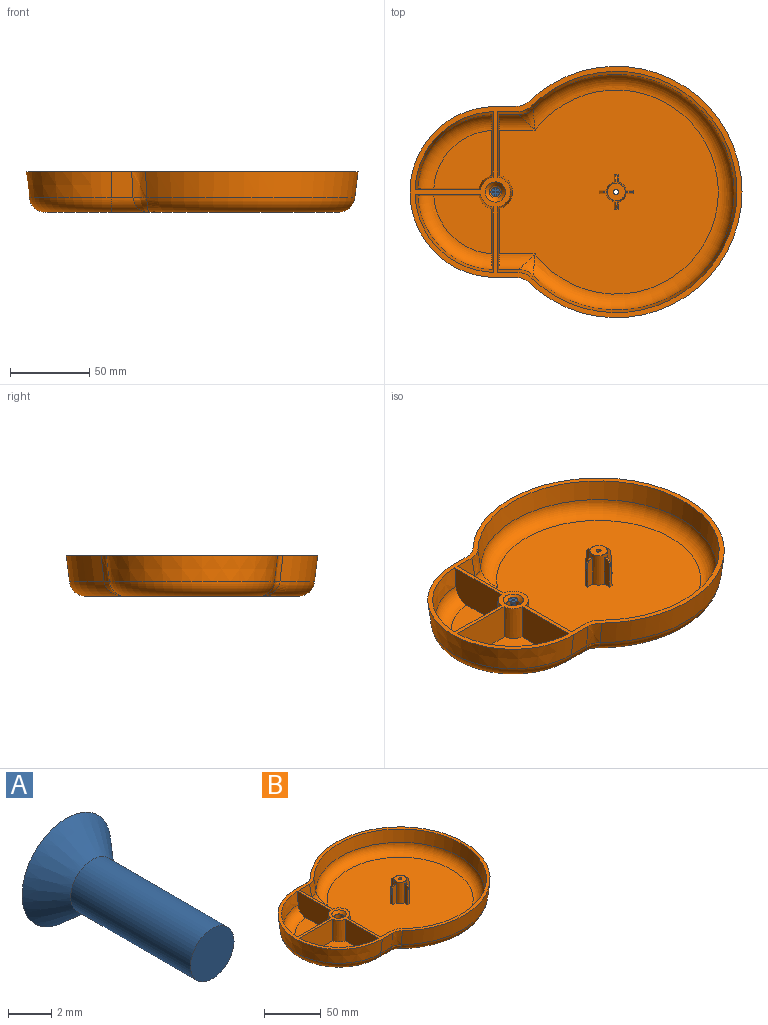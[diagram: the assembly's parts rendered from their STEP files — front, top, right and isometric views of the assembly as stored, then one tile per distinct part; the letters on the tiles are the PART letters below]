
ASSEMBLY  parts=2 mates=1
PART A: 17 faces, bbox 5.8x9.5x5.8 mm
  f0: plane 5.8x5.8mm, normal (0,1,0), area 20.5mm2, adj f1,f2,f5,f6,f8,f9,f10,f11
  f1: plane 1.78x0.38mm, normal (-1,0,0), area 0.7mm2, adj f0,f6,f7,f8
  f2: plane 1.78x0.38mm, normal (1,0,0), area 0.7mm2, adj f0,f6,f7,f10
  f3: plane 2.85x2.85mm, normal (0,-1,0), area 6.4mm2, adj f4
  f4: cylinder r=1.42mm len=7.82mm, axis (0,1,0), area 69.9mm2, adj f3,f5
  f5: cone r=1.42mm half-angle=41deg, axis (0,1,0), area 30.6mm2, adj f0,f4
  f6: plane 0.76x0.38mm, normal (0,0,-1), area 0.3mm2, adj f0,f1,f2,f7
  f7: plane 4.32x4.32mm, normal (0,1,0), area 6mm2, adj f1,f2,f6,f8,f9,f10,f11,f12
  f8: plane 1.78x0.38mm, normal (0,0,-1), area 0.7mm2, adj f0,f1,f7,f16
  f9: plane 1.78x0.38mm, normal (0,0,1), area 0.7mm2, adj f0,f7,f11,f12
  f10: plane 1.78x0.38mm, normal (0,0,-1), area 0.7mm2, adj f0,f2,f7,f11
  f11: plane 0.76x0.38mm, normal (1,0,0), area 0.3mm2, adj f0,f7,f9,f10
  f12: plane 1.78x0.38mm, normal (1,0,0), area 0.7mm2, adj f0,f7,f9,f14
  f13: plane 1.78x0.38mm, normal (-1,0,0), area 0.7mm2, adj f0,f7,f14,f15
  f14: plane 0.76x0.38mm, normal (0,0,1), area 0.3mm2, adj f0,f7,f12,f13
  f15: plane 1.78x0.38mm, normal (0,0,1), area 0.7mm2, adj f0,f7,f13,f16
  f16: plane 0.76x0.38mm, normal (-1,0,0), area 0.3mm2, adj f0,f7,f8,f15
PART B: 68 faces, bbox 216.5x167.7x161.1 mm
  f0: cone r=47.65mm half-angle=7deg, axis (0,0,1), area 1007.1mm2, adj f1,f12,f34,f38
  f1: torus R=39mm, axis (0,0,1), area 976.5mm2, adj f0,f2,f34,f38
  f2: plane 36.49x36.49mm, normal (0,0,1), area 966.8mm2, adj f1,f3,f34,f38
  f3: cone r=9.53mm half-angle=3deg, axis (0,0,-1), area 271.2mm2, adj f2,f12,f34,f38
  f4: cone r=47.65mm half-angle=7deg, axis (0,0,1), area 1007.1mm2, adj f6,f12,f35,f37
  f5: plane 36.49x36.49mm, normal (0,0,1), area 966.8mm2, adj f6,f7,f35,f37
  f6: torus R=39mm, axis (0,0,1), area 976.5mm2, adj f4,f5,f35,f37
  f7: cone r=9.53mm half-angle=3deg, axis (0,0,-1), area 271.2mm2, adj f5,f12,f35,f37
  f8: plane 16.48x13.58mm, normal (0,-0.99,-0.12), area 218.6mm2, adj f11,f12,f18,f29
  f9: cone r=76.2mm half-angle=7deg, axis (0,0,1), area 6076.3mm2, adj f12,f20,f29,f31
  f10: plane 16.48x13.58mm, normal (0,0.99,-0.12), area 218.6mm2, adj f11,f12,f21,f31
  f11: cone r=50.8mm half-angle=7deg, axis (0,0,1), area 2759.5mm2, adj f8,f10,f12,f19
  f12: plane 209.69x158.89mm, normal (0,0,1), area 2312.5mm2, adj f0,f3,f4,f7,f8,f9,f10,f11
  f13: plane 185.22x134.42mm, normal (0,0,-1), area 18002.1mm2, adj f18,f19,f20,f21,f65
  f14: plane 13.46x13.3mm, normal (0,0.99,0.12), area 171.2mm2, adj f12,f24,f27,f39
  f15: cone r=73.05mm half-angle=7deg, axis (0,0,1), area 4744.9mm2, adj f12,f22,f25,f27
  f16: plane 13.46x13.3mm, normal (0,-0.99,0.12), area 171.2mm2, adj f12,f23,f25,f36
  f17: plane 138.17x128.8mm, normal (0,0,1), area 13789.8mm2, adj f22,f23,f24,f33,f36,f39,f43,f45
  f18: cylinder r=10.16mm len=23.58mm, axis (-1,0,0), area 273.4mm2, adj f8,f13,f19,f30
  f19: torus R=41.81mm, axis (0,0,1), area 2218mm2, adj f11,f13,f18,f21
  f20: torus R=67.21mm, axis (0,0,1), area 5192.6mm2, adj f9,f13,f30,f32
  f21: cylinder r=10.16mm len=23.58mm, axis (-1,0,0), area 273.4mm2, adj f10,f13,f19,f32
  f22: torus R=64.4mm, axis (0,0,1), area 5028.6mm2, adj f15,f17,f26,f28
  f23: cylinder r=10.16mm len=22.98mm, axis (1,0,0), area 259.6mm2, adj f16,f17,f26,f36
  f24: cylinder r=10.16mm len=22.98mm, axis (1,0,0), area 259.6mm2, adj f14,f17,f28,f39
  f25: bspline ~126.22x18.65mm, area 131.8mm2, adj f12,f15,f16,f26
  f26: bspline ~13.84x10.28mm, area 60.5mm2, adj f22,f23,f25
  f27: bspline ~155.52x22.25mm, area 131.8mm2, adj f12,f14,f15,f28
  f28: bspline ~13.84x10.28mm, area 60.5mm2, adj f22,f24,f27
  f29: bspline ~130.53x19.08mm, area 160.5mm2, adj f8,f9,f12,f30
  f30: bspline ~13.73x10.06mm, area 59.3mm2, adj f18,f20,f29
  f31: bspline ~160.83x22.8mm, area 160.4mm2, adj f9,f10,f12,f32
  f32: bspline ~13.73x10.06mm, area 59.3mm2, adj f20,f21,f31
  f33: cone r=9.53mm half-angle=3deg, axis (0,0,-1), area 624.5mm2, adj f12,f17,f36,f39
  f34: plane 41.36x22.32mm, normal (0,-1,0.05), area 860mm2, adj f0,f1,f2,f3,f12
  f35: plane 41.36x22.32mm, normal (0,1,0.05), area 860mm2, adj f4,f5,f6,f7,f12
  f36: plane 41.48x22.43mm, normal (1,0,0.05), area 860.8mm2, adj f12,f16,f17,f23,f33
  f37: plane 41.36x22.32mm, normal (-1,0,0.05), area 860mm2, adj f4,f5,f6,f7,f12
  f38: plane 41.36x22.32mm, normal (-1,0,0.05), area 860mm2, adj f0,f1,f2,f3,f12
  f39: plane 41.48x22.43mm, normal (1,0,0.05), area 860.8mm2, adj f12,f14,f17,f24,f33
  f40: cone r=0mm half-angle=59deg, axis (0,0,1), area 59mm2, adj f41
  f41: cylinder r=4.01mm len=16.36mm, axis (0,0,1), area 412.6mm2, adj f40,f42
  f42: cone r=4.01mm half-angle=41deg, axis (0,0,1), area 116mm2, adj f12,f41
  f43: cone r=5.56mm half-angle=2deg, axis (0,0,-1), area 697.6mm2, adj f17,f44,f45,f46,f47,f49,f50,f51
  f44: plane 11.11x11.11mm, normal (0,0,1), area 89.1mm2, adj f43,f67
  f45: plane 19.72x5.26mm, normal (1,0,0.03), area 88.1mm2, adj f17,f43,f47,f48,f64
  f46: plane 19.72x5.26mm, normal (-1,0,0.03), area 88.1mm2, adj f17,f43,f47,f48,f64
  f47: plane 2.51x1.02mm, normal (0,0,1), area 2.5mm2, adj f43,f45,f46,f64
  f48: plane 17.65x2.39mm, normal (0,1,0.03), area 31.3mm2, adj f17,f45,f46,f64
  f49: plane 2.51x1.02mm, normal (0,0,1), area 2.5mm2, adj f43,f50,f51,f61
  f50: plane 19.72x5.26mm, normal (0,-1,0.03), area 88.1mm2, adj f17,f43,f49,f52,f61
  f51: plane 19.72x5.26mm, normal (0,1,0.03), area 88.1mm2, adj f17,f43,f49,f52,f61
  f52: plane 17.65x2.39mm, normal (1,0,0.03), area 31.3mm2, adj f17,f50,f51,f61
  f53: plane 2.51x1.02mm, normal (0,0,1), area 2.5mm2, adj f43,f54,f55,f63
  f54: plane 19.72x5.26mm, normal (0,1,0.03), area 88.1mm2, adj f17,f43,f53,f56,f63
  f55: plane 19.72x5.26mm, normal (0,-1,0.03), area 88.1mm2, adj f17,f43,f53,f56,f63
  f56: plane 17.65x2.39mm, normal (-1,0,0.03), area 31.3mm2, adj f17,f54,f55,f63
  f57: plane 2.51x1.02mm, normal (0,0,1), area 2.5mm2, adj f43,f58,f60,f62
  f58: plane 19.72x5.26mm, normal (1,0,0.03), area 88.1mm2, adj f17,f43,f57,f59,f62
  f59: plane 17.65x2.39mm, normal (0,-1,0.03), area 31.3mm2, adj f17,f58,f60,f62
  f60: plane 19.72x5.26mm, normal (-1,0,0.03), area 88.1mm2, adj f17,f43,f57,f59,f62
  f61: plane 2.1x2.03mm, normal (0.69,0,0.72), area 3.2mm2, adj f49,f50,f51,f52
  f62: plane 2.1x2.03mm, normal (0,-0.69,0.72), area 3.2mm2, adj f57,f58,f59,f60
  f63: plane 2.1x2.03mm, normal (-0.69,0,0.72), area 3.2mm2, adj f53,f54,f55,f56
  f64: plane 2.1x2.03mm, normal (0,0.69,0.72), area 3.2mm2, adj f45,f46,f47,f48
  f65: cone r=4.03mm half-angle=2deg, axis (0,0,-1), area 667.9mm2, adj f13,f66
  f66: plane 8.06x8.06mm, normal (0,0,-1), area 42.6mm2, adj f65,f67
  f67: cone r=1.59mm half-angle=2deg, axis (0,0,-1), area 15.5mm2, adj f44,f66
PLACE A rot(axis=(1,0,0),90deg) t=(0,0,15.88)mm
PLACE B at identity
MATE fastened A.f4 <-> B.f0  axis (0,0,1) through (0,0,25.4)mm
